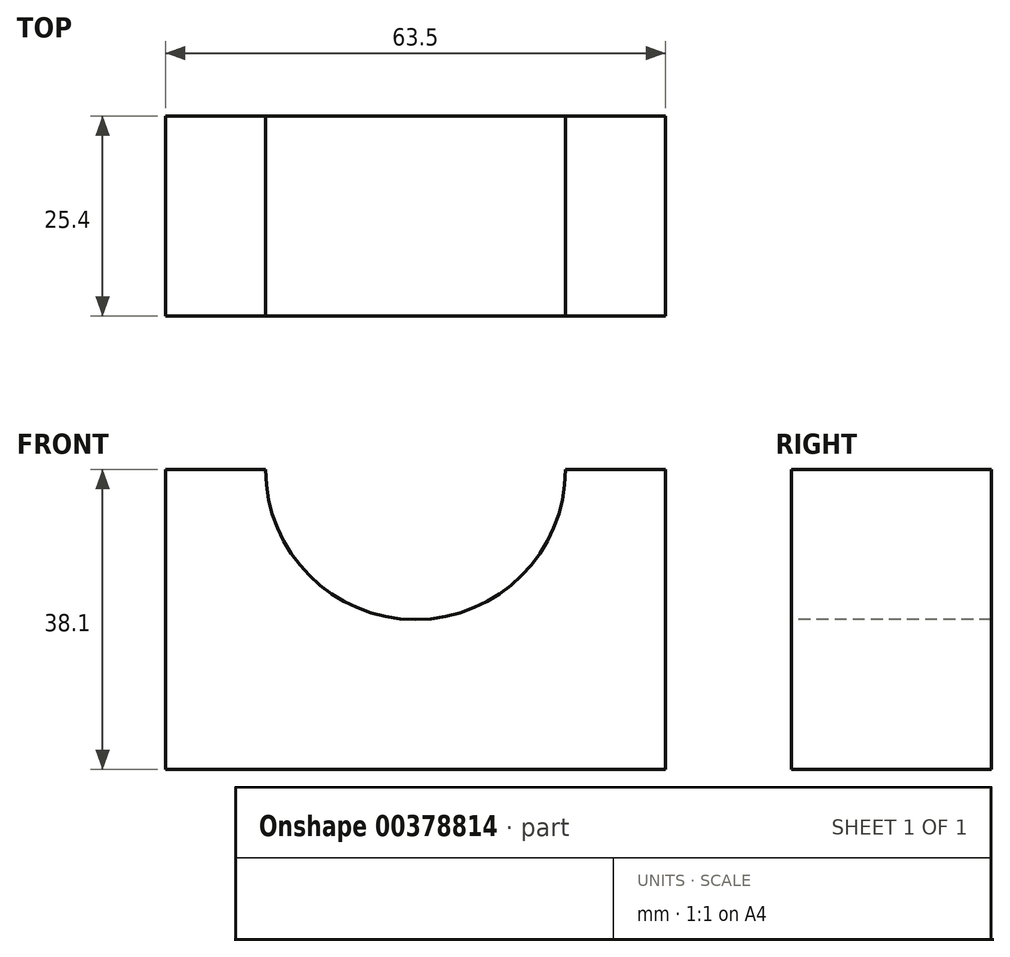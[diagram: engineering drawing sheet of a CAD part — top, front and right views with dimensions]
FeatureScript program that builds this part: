
annotation { "Feature Type Name" : "Feature", "Feature Type Description" : "" }
export const myFeature = defineFeature(function(context is Context, id is Id, definition is map)
    precondition{}
    {
        {
            var Q0;
            Q0=qCreatedBy(makeId("Front.planeOp"),FACE);
            var sketch = newSketch(context, id + "F0", { "sketchPlane" : qUnion([Q0])});
            skLineSegment(sketch, "E0", {"start": v(0, 0) * mm, "end": v(63.5, 0) * mm});
            skLineSegment(sketch, "E1", {"start": v(63.5, 0) * mm, "end": v(63.5, 38.1) * mm});
            skLineSegment(sketch, "E2", {"start": v(63.5, 38.1) * mm, "end": v(0, 38.1) * mm});
            skLineSegment(sketch, "E3", {"start": v(0, 38.1) * mm, "end": v(0, 0) * mm});
            skSolve(sketch);
        }
        {
            var Q0;
            Q0 = qSketchRegion(id + "F0", true);
            extrude(context, id + "F1", {"entities" : qUnion([Q0]), "depth" : 25.4 * mm});
        }
        {
            var Q0;
            Q0=makeQuery(id+"F1.opExtrude","CAP_FACE",FACE,{"disambiguationData":[OSD([sQuery(id+"F0.wireOp",EDGE,"E0"),sQuery(id+"F0.wireOp",EDGE,"E1"),sQuery(id+"F0.wireOp",EDGE,"E2"),sQuery(id+"F0.wireOp",EDGE,"E3")])],"isStart":false});
            var sketch = newSketch(context, id + "F2", { "sketchPlane" : qUnion([Q0])});
            skCircle(sketch, "E4", {"center": v(31.75, 38.1) * mm, "radius": 19.05 * mm});
            skSolve(sketch);
        }
        {
            var Q0;
            {var subQ0=sQuery(id+"F2.wireOp",EDGE,"E4");var subQ1=makeQuery(id+"F1.opExtrude","CAP_EDGE",EDGE,{"disambiguationData":[OSD([sQuery(id+"F0.wireOp",EDGE,"E2")])],"isStart":false});var subQ2=makeQuery(id+"F2.imprint","INTERSECT",VERTEX,{"disambiguationData":[OD(0.0)],"derivedFrom":[subQ1,subQ0]});Q0=makeQuery(id+"F2.imprint","IMPRINT",FACE,{"disambiguationData":[TD([[makeQuery(id+"F2.imprint","IMPRINT",EDGE,{"disambiguationData":[TD([[subQ2,-1.0]])],"derivedFrom":subQ0}),1.0]])]});}
            var Q1;
            {var subQ0=sQuery(id+"F2.wireOp",EDGE,"E4");var subQ1=makeQuery(id+"F1.opExtrude","CAP_EDGE",EDGE,{"disambiguationData":[OSD([sQuery(id+"F0.wireOp",EDGE,"E2")])],"isStart":false});var subQ2=makeQuery(id+"F2.imprint","INTERSECT",VERTEX,{"disambiguationData":[OD(0.0)],"derivedFrom":[subQ1,subQ0]});Q1=makeQuery(id+"F2.imprint","IMPRINT",FACE,{"disambiguationData":[TD([[makeQuery(id+"F2.imprint","IMPRINT",EDGE,{"disambiguationData":[TD([[subQ2,1.0]])],"derivedFrom":subQ0}),1.0]])]});}
            extrude(context, id + "F3", {"entities" : qUnion([Q0, Q1]), "operationType" : NewBodyOperationType.REMOVE, "oppositeDirection" : true, "depth" : 25.4 * mm});
        }
    });
